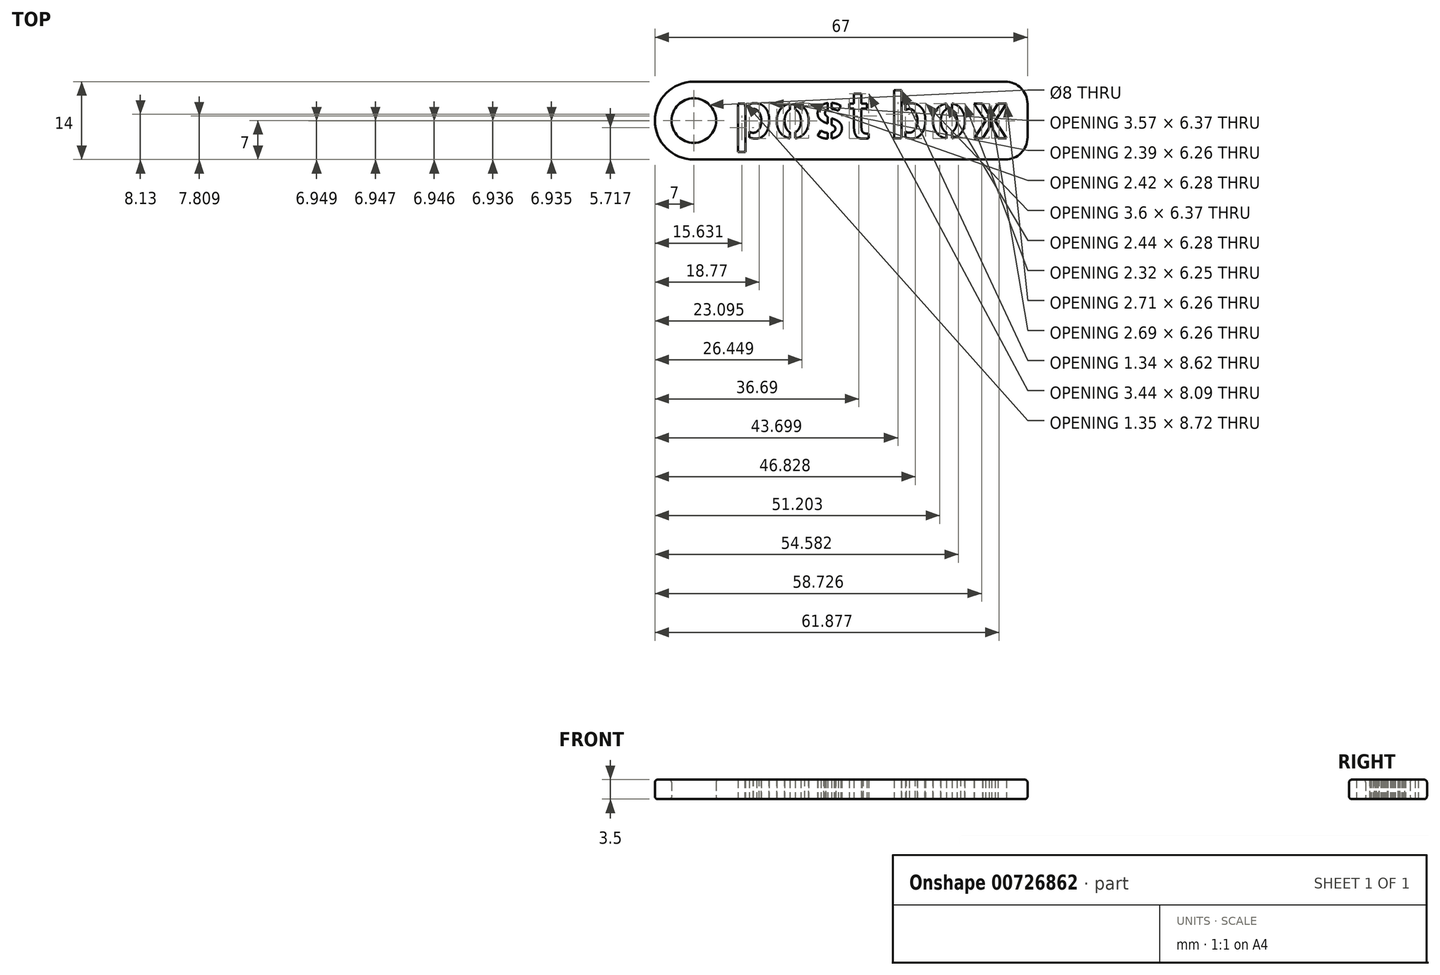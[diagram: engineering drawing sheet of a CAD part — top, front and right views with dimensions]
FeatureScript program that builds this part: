
annotation { "Feature Type Name" : "Feature", "Feature Type Description" : "" }
export const myFeature = defineFeature(function(context is Context, id is Id, definition is map)
    precondition{}
    {
        {
            var Q0;
            Q0=qCreatedBy(makeId("Top.planeOp"),FACE);
            var sketch = newSketch(context, id + "F0", { "sketchPlane" : qUnion([Q0])});
            skLineSegment(sketch, "E0.bottom", {"start": v(0, 0) * mm, "end": v(60, 0) * mm});
            skLineSegment(sketch, "E0.top", {"start": v(0, -14) * mm, "end": v(60, -14) * mm});
            skLineSegment(sketch, "E0.left", {"start": v(0, 0) * mm, "end": v(0, -14) * mm});
            skLineSegment(sketch, "E0.right", {"start": v(60, 0) * mm, "end": v(60, -14) * mm});
            skArc(sketch, "E1", {"start": v(0, 0) * mm, "mid": v(-7, -7) * mm, "end": v(0, -14) * mm});
            skCircle(sketch, "E2", {"center": v(0, -7) * mm, "radius": 4 * mm});
            skText(sketch, "E3", { "text": "post box", "fontName": "AllertaStencil-Regular.ttf"});
            skLineSegment(sketch, "E4", {"start": v(9.98, -3.62) * mm, "end": v(9.98, -11.22) * mm});
            skLineSegment(sketch, "E5", {"start": v(17.29, -3.38) * mm, "end": v(17.29, -11.22) * mm});
            skLineSegment(sketch, "E6", {"start": v(18.24, -3.2) * mm, "end": v(18.24, -11.22) * mm});
            skLineSegment(sketch, "E7", {"start": v(38.03, -3.76) * mm, "end": v(38.03, -10.86) * mm});
            skLineSegment(sketch, "E8", {"start": v(45.42, -3.48) * mm, "end": v(45.42, -10.86) * mm});
            skLineSegment(sketch, "E9", {"start": v(46.42, -3.43) * mm, "end": v(46.42, -10.86) * mm});
            skLineSegment(sketch, "E10", {"start": v(24.07, -3.34) * mm, "end": v(24.07, -11.06) * mm});
            skLineSegment(sketch, "E11", {"start": v(24.8, -3.27) * mm, "end": v(24.8, -11.06) * mm});
            const initialGuessF0  = {"E3": [0.007, -0.01018, 1, 0, 0.00818]};
            skSetInitialGuess(sketch, initialGuessF0);
            skSolve(sketch);
        }
        {
            var Q0;
            {var subQ0=sQuery(id+"F0.wireOp",EDGE,"E1");Q0=makeQuery(id+"F0.imprint","IMPRINT",FACE,{"disambiguationData":[TD([[makeQuery(id+"F0.imprint","IMPRINT",EDGE,{"derivedFrom":subQ0}),1.0]])]});}
            var Q1;
            {var subQ0=sQuery(id+"F0.wireOp",EDGE,"E3.sketch_text.stroke-12");Q1=makeQuery(id+"F0.imprint","IMPRINT",FACE,{"disambiguationData":[TD([[makeQuery(id+"F0.imprint","IMPRINT",EDGE,{"derivedFrom":subQ0}),-1.0]])]});}
            var Q2;
            {var subQ0=sQuery(id+"F0.wireOp",EDGE,"E3.sketch_text.stroke-24");Q2=makeQuery(id+"F0.imprint","IMPRINT",FACE,{"disambiguationData":[TD([[makeQuery(id+"F0.imprint","IMPRINT",EDGE,{"derivedFrom":subQ0}),-1.0]])]});}
            var Q3;
            {var subQ0=sQuery(id+"F0.wireOp",EDGE,"E3.sketch_text.stroke-51");Q3=makeQuery(id+"F0.imprint","IMPRINT",FACE,{"disambiguationData":[TD([[makeQuery(id+"F0.imprint","IMPRINT",EDGE,{"derivedFrom":subQ0}),-1.0]])]});}
            var Q4;
            {var subQ0=sQuery(id+"F0.wireOp",EDGE,"E3.sketch_text.stroke-46");Q4=makeQuery(id+"F0.imprint","IMPRINT",FACE,{"disambiguationData":[TD([[makeQuery(id+"F0.imprint","IMPRINT",EDGE,{"derivedFrom":subQ0}),-1.0]])]});}
            var Q5;
            {var subQ0=sQuery(id+"F0.wireOp",EDGE,"E3.sketch_text.stroke-58");Q5=makeQuery(id+"F0.imprint","IMPRINT",FACE,{"disambiguationData":[TD([[makeQuery(id+"F0.imprint","IMPRINT",EDGE,{"derivedFrom":subQ0}),-1.0]])]});}
            var Q6;
            {var subQ0=sQuery(id+"F0.wireOp",EDGE,"E3.sketch_text.stroke-39");Q6=makeQuery(id+"F0.imprint","IMPRINT",FACE,{"disambiguationData":[TD([[makeQuery(id+"F0.imprint","IMPRINT",EDGE,{"derivedFrom":subQ0}),-1.0]])]});}
            var Q7;
            {var subQ5=sQuery(id+"F0.wireOp",EDGE,"E3.sketch_text.stroke-41");Q7=makeQuery(id+"F0.imprint","IMPRINT",FACE,{"disambiguationData":[TD([[makeQuery(id+"F0.imprint","IMPRINT",EDGE,{"derivedFrom":subQ5}),1.0]])]});}
            var Q8;
            {var subQ0=sQuery(id+"F0.wireOp",EDGE,"E3.sketch_text.stroke-53");Q8=makeQuery(id+"F0.imprint","IMPRINT",FACE,{"disambiguationData":[TD([[makeQuery(id+"F0.imprint","IMPRINT",EDGE,{"derivedFrom":subQ0}),1.0]])]});}
            var Q9;
            {var subQ0=sQuery(id+"F0.wireOp",EDGE,"E3.sketch_text.stroke-157");Q9=makeQuery(id+"F0.imprint","IMPRINT",FACE,{"disambiguationData":[TD([[makeQuery(id+"F0.imprint","IMPRINT",EDGE,{"derivedFrom":subQ0}),-1.0]])]});}
            var Q10;
            {var subQ0=sQuery(id+"F0.wireOp",EDGE,"E3.sketch_text.stroke-144");Q10=makeQuery(id+"F0.imprint","IMPRINT",FACE,{"disambiguationData":[TD([[makeQuery(id+"F0.imprint","IMPRINT",EDGE,{"derivedFrom":subQ0}),-1.0]])]});}
            var Q11;
            {var subQ0=sQuery(id+"F0.wireOp",EDGE,"E3.sketch_text.stroke-184");Q11=makeQuery(id+"F0.imprint","IMPRINT",FACE,{"disambiguationData":[TD([[makeQuery(id+"F0.imprint","IMPRINT",EDGE,{"derivedFrom":subQ0}),-1.0]])]});}
            var Q12;
            {var subQ0=sQuery(id+"F0.wireOp",EDGE,"E3.sketch_text.stroke-179");Q12=makeQuery(id+"F0.imprint","IMPRINT",FACE,{"disambiguationData":[TD([[makeQuery(id+"F0.imprint","IMPRINT",EDGE,{"derivedFrom":subQ0}),-1.0]])]});}
            var Q13;
            {var subQ0=sQuery(id+"F0.wireOp",EDGE,"E3.sketch_text.stroke-191");Q13=makeQuery(id+"F0.imprint","IMPRINT",FACE,{"disambiguationData":[TD([[makeQuery(id+"F0.imprint","IMPRINT",EDGE,{"derivedFrom":subQ0}),-1.0]])]});}
            var Q14;
            {var subQ0=sQuery(id+"F0.wireOp",EDGE,"E3.sketch_text.stroke-172");Q14=makeQuery(id+"F0.imprint","IMPRINT",FACE,{"disambiguationData":[TD([[makeQuery(id+"F0.imprint","IMPRINT",EDGE,{"derivedFrom":subQ0}),-1.0]])]});}
            var Q15;
            {var subQ0=sQuery(id+"F0.wireOp",EDGE,"E3.sketch_text.stroke-186");Q15=makeQuery(id+"F0.imprint","IMPRINT",FACE,{"disambiguationData":[TD([[makeQuery(id+"F0.imprint","IMPRINT",EDGE,{"derivedFrom":subQ0}),1.0]])]});}
            var Q16;
            {var subQ5=sQuery(id+"F0.wireOp",EDGE,"E3.sketch_text.stroke-174");Q16=makeQuery(id+"F0.imprint","IMPRINT",FACE,{"disambiguationData":[TD([[makeQuery(id+"F0.imprint","IMPRINT",EDGE,{"derivedFrom":subQ5}),1.0]])]});}
            var Q17;
            {var subQ62=sQuery(id+"F0.wireOp",EDGE,"E0.bottom");Q17=makeQuery(id+"F0.imprint","IMPRINT",FACE,{"disambiguationData":[TD([[makeQuery(id+"F0.imprint","IMPRINT",EDGE,{"derivedFrom":subQ62}),-1.0]])]});}
            var Q18;
            {var subQ1=sQuery(id+"F0.wireOp",EDGE,"E3.sketch_text.stroke-14");Q18=makeQuery(id+"F0.imprint","IMPRINT",FACE,{"disambiguationData":[TD([[makeQuery(id+"F0.imprint","IMPRINT",EDGE,{"derivedFrom":subQ1}),1.0]])]});}
            var Q19;
            {var subQ0=sQuery(id+"F0.wireOp",EDGE,"E3.sketch_text.stroke-146");Q19=makeQuery(id+"F0.imprint","IMPRINT",FACE,{"disambiguationData":[TD([[makeQuery(id+"F0.imprint","IMPRINT",EDGE,{"derivedFrom":subQ0}),1.0]])]});}
            var Q20;
            {var subQ0=sQuery(id+"F0.wireOp",EDGE,"E3.sketch_text.stroke-67");Q20=makeQuery(id+"F0.imprint","IMPRINT",FACE,{"disambiguationData":[TD([[makeQuery(id+"F0.imprint","IMPRINT",EDGE,{"derivedFrom":subQ0}),-1.0]])]});}
            var Q21;
            {var subQ0=sQuery(id+"F0.wireOp",EDGE,"E3.sketch_text.stroke-79");Q21=makeQuery(id+"F0.imprint","IMPRINT",FACE,{"disambiguationData":[TD([[makeQuery(id+"F0.imprint","IMPRINT",EDGE,{"derivedFrom":subQ0}),-1.0]])]});}
            var Q22;
            {var subQ0=sQuery(id+"F0.wireOp",EDGE,"E3.sketch_text.stroke-72");Q22=makeQuery(id+"F0.imprint","IMPRINT",FACE,{"disambiguationData":[TD([[makeQuery(id+"F0.imprint","IMPRINT",EDGE,{"derivedFrom":subQ0}),-1.0]])]});}
            var Q23;
            {var subQ0=sQuery(id+"F0.wireOp",EDGE,"E3.sketch_text.stroke-105");Q23=makeQuery(id+"F0.imprint","IMPRINT",FACE,{"disambiguationData":[TD([[makeQuery(id+"F0.imprint","IMPRINT",EDGE,{"derivedFrom":subQ0}),-1.0]])]});}
            var Q24;
            {var subQ4=sQuery(id+"F0.wireOp",EDGE,"E3.sketch_text.stroke-69");Q24=makeQuery(id+"F0.imprint","IMPRINT",FACE,{"disambiguationData":[TD([[makeQuery(id+"F0.imprint","IMPRINT",EDGE,{"derivedFrom":subQ4}),1.0]])]});}
            var Q25;
            {var subQ6=sQuery(id+"F0.wireOp",EDGE,"E3.sketch_text.stroke-102");Q25=makeQuery(id+"F0.imprint","IMPRINT",FACE,{"disambiguationData":[TD([[makeQuery(id+"F0.imprint","IMPRINT",EDGE,{"derivedFrom":subQ6}),1.0]])]});}
            var Q26;
            {var subQ4=sQuery(id+"F0.wireOp",EDGE,"E3.sketch_text.stroke-85");Q26=makeQuery(id+"F0.imprint","IMPRINT",FACE,{"disambiguationData":[TD([[makeQuery(id+"F0.imprint","IMPRINT",EDGE,{"derivedFrom":subQ4}),-1.0]])]});}
            var Q27;
            {var subQ0=sQuery(id+"F0.wireOp",EDGE,"E3.sketch_text.stroke-100");Q27=makeQuery(id+"F0.imprint","IMPRINT",FACE,{"disambiguationData":[TD([[makeQuery(id+"F0.imprint","IMPRINT",EDGE,{"derivedFrom":subQ0}),-1.0]])]});}
            extrude(context, id + "F1", {"entities" : qUnion([Q0, Q1, Q2, Q3, Q4, Q5, Q6, Q7, Q8, Q9, Q10, Q11, Q12, Q13, Q14, Q15, Q16, Q17, Q18, Q19, Q20, Q21, Q22, Q23, Q24, Q25, Q26, Q27]), "depth" : 3.5 * mm, "offsetDistance" : 25 * mm});
        }
        {
            var Q0;
            Q0=makeQuery(id+"F1.opExtrude","CAP_EDGE",EDGE,{"disambiguationData":[OSD([sQuery(id+"F0.wireOp",EDGE,"E2")])],"isStart":false});
            var Q1;
            Q1=makeQuery(id+"F1.opExtrude","CAP_EDGE",EDGE,{"disambiguationData":[OSD([sQuery(id+"F0.wireOp",EDGE,"E2")])],"isStart":true});
            var Q2;
            Q2=makeQuery(id+"F1.opExtrude","CAP_EDGE",EDGE,{"disambiguationData":[OSD([sQuery(id+"F0.wireOp",EDGE,"E0.bottom")])],"isStart":true});
            var Q3;
            Q3=makeQuery(id+"F1.opExtrude","CAP_EDGE",EDGE,{"disambiguationData":[OSD([sQuery(id+"F0.wireOp",EDGE,"E0.right")])],"isStart":true});
            var Q4;
            Q4=makeQuery(id+"F1.opExtrude","CAP_EDGE",EDGE,{"disambiguationData":[OSD([sQuery(id+"F0.wireOp",EDGE,"E0.bottom")])],"isStart":false});
            var Q5;
            Q5=makeQuery(id+"F1.opExtrude","CAP_EDGE",EDGE,{"disambiguationData":[OSD([sQuery(id+"F0.wireOp",EDGE,"E0.right")])],"isStart":false});
            fillet(context, id + "F2", {"entities" : qUnion([Q0, Q1, Q2, Q3, Q4, Q5]), "radius" : 0.5 * mm, "tangentPropagation" : true, "allowEdgeOverflow" : false});
        }
        {
            var Q0;
            Q0=makeQuery(id+"F1.opExtrude","SWEPT_EDGE",EDGE,{"disambiguationData":[OSD([sQuery(id+"F0.wireOp",EDGE,"E0.top"),sQuery(id+"F0.wireOp",EDGE,"E0.right")])]});
            var Q1;
            Q1=makeQuery(id+"F1.opExtrude","SWEPT_EDGE",EDGE,{"disambiguationData":[OSD([sQuery(id+"F0.wireOp",EDGE,"E0.bottom"),sQuery(id+"F0.wireOp",EDGE,"E0.right")])]});
            fillet(context, id + "F3", {"entities" : qUnion([Q0, Q1]), "radius" : 4 * mm, "tangentPropagation" : true, "allowEdgeOverflow" : false});
        }
    });
